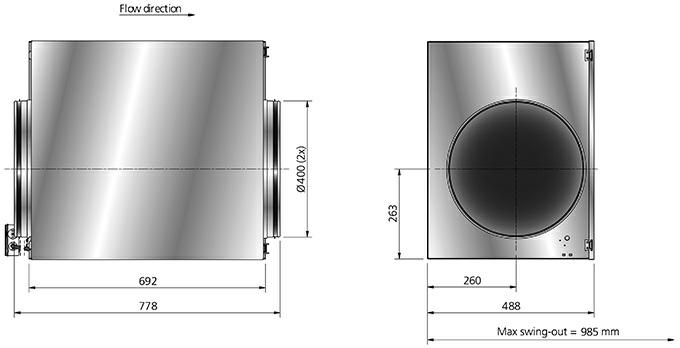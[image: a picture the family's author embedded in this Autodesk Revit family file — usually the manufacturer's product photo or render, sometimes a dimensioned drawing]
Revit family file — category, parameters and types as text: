
# Revit family: IRE 500 A3 ErP AC_7900036
name_source: partatom
category: Mechanical Equipment
revit_build: Autodesk Revit MEP 2014 (Build: 20130308_1515(x64)
units: mm (PartAtom-declared; Revit-internal decimal feet)

## types (1)
- IRE 500 A3 ErP AC
    Capacitor = - μF
    Current = 2 A
    Depth = 780 mm  [stored 2.55906 ft]
    Description = Insulated duct fans with circular connections
    Diameter = 500 mm  [stored 1.64042 ft]
    Frequency = 50 Hz
    Height = 584 mm  [stored 1.91601 ft]
    Main Material = Steel, Galvanized
    Max. temperature of transported air = 90 °C
    Max. temperature of transported air when speed controlled = 90 °C
    Phase = 3
    Power = 540 W
    Sound pressure level at 3 m = 42 dB(A)
    Speed = 690 rpm
    Voltage = 400 V
    Voltage range = 380-415 V
    Weight = 71.40 kg
    Width = 907 mm  [stored 2.97572 ft]
    Wiring diagram = Y 4040004 / Δ 4040003

note: [stored X ft] marks values corroborated as IEEE doubles in the binary element streams (Revit-internal decimal feet)

## geometry (parser evidence)
native form markers: Sweep x5
no freeform markers — native parametric forms only
